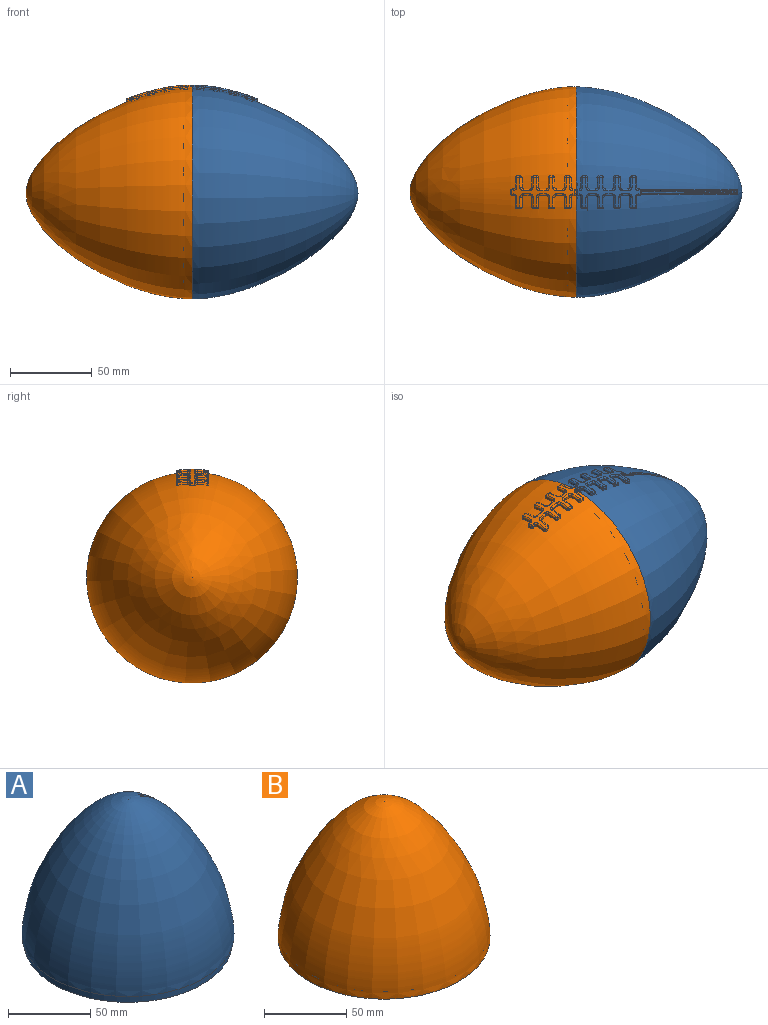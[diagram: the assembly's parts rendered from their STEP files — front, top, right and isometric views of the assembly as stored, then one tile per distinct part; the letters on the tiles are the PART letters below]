
ASSEMBLY  parts=2 mates=1
PART A: 160 faces, bbox 131.7x129.7x107.3 mm
  f0: revolved ~129.02x129.02mm, area 33050.8mm2, adj f1,f83,f84,f85,f86,f87,f88,f89
  f1: bspline ~64.71x52.04mm, area 63.7mm2, adj f0,f2,f83,f159
  f2: plane 59.61x48.72mm, normal (0,1,0), area 17.4mm2, adj f1,f3,f7,f159
  f3: bspline ~63.77x53.46mm, area 64.3mm2, adj f2,f4,f7,f159
  f4: revolved ~58.94x49.24mm, area 78mm2, adj f3,f5,f7,f159
  f5: bspline ~63.77x53.46mm, area 64.2mm2, adj f4,f6,f7,f159
  f6: plane 59.63x48.75mm, normal (0,-1,0), area 17.9mm2, adj f5,f7,f158,f159
  f7: plane 2.57x2.1mm, normal (0,0,1), area 4.8mm2, adj f2,f3,f4,f5,f6,f8,f83,f157
  f8: torus R=55.47mm, axis (0,0,1), area 2.4mm2, adj f7,f9,f81,f82
  f9: revolved ~128.83x128.74mm, area 10804.2mm2, adj f8,f10,f11,f13,f15,f16,f17,f18
  f10: bspline ~2.48x2.39mm, area 3.2mm2, adj f9,f11,f80,f101
  f11: torus R=62mm, axis (0,0,1), area 8.5mm2, adj f9,f10,f12,f102
  f12: sphere r=1mm, area 1.3mm2, adj f11,f13,f103
  f13: bspline ~11.59x3.03mm, area 2.9mm2, adj f9,f12,f14,f104
  f14: sphere r=1mm, area 2.1mm2, adj f13,f15,f105
  f15: torus R=62.34mm, axis (0,0,1), area 10.5mm2, adj f9,f14,f16,f106
  f16: bspline ~2.48x2.37mm, area 3.6mm2, adj f9,f15,f17,f107
  f17: bspline ~11.23x2.39mm, area 6.3mm2, adj f9,f16,f18,f108
  f18: bspline ~2.48x2.38mm, area 3.3mm2, adj f9,f17,f19,f109
  f19: torus R=63.28mm, axis (0,0,1), area 9.1mm2, adj f9,f18,f20,f110
  f20: sphere r=1mm, area 1.4mm2, adj f19,f21,f111
  f21: bspline ~8.41x1.67mm, area 2.9mm2, adj f9,f20,f22,f112
  f22: sphere r=1mm, area 1.5mm2, adj f21,f23,f113
  f23: torus R=63.41mm, axis (0,0,1), area 9.9mm2, adj f9,f22,f24,f114
  f24: bspline ~2.49x2.38mm, area 3.4mm2, adj f9,f23,f25,f115
  f25: bspline ~6.99x1.31mm, area 1.6mm2, adj f9,f24,f26,f116
  f26: sphere r=1mm, area 1.6mm2, adj f25,f27,f117
  f27: torus R=63.5mm, axis (0,0,1), area 3.2mm2, adj f9,f26,f28,f118
  f28: sphere r=1mm, area 1.6mm2, adj f27,f29,f123
  f29: bspline ~6.99x1.32mm, area 1.6mm2, adj f9,f28,f30,f124
  f30: bspline ~2.48x2.38mm, area 3.4mm2, adj f9,f29,f31,f125
  f31: torus R=63.41mm, axis (0,0,1), area 9.9mm2, adj f9,f30,f32,f126
  f32: sphere r=1mm, area 0.9mm2, adj f31,f33,f127
  f33: bspline ~8.41x1.67mm, area 2.9mm2, adj f9,f32,f34,f128
  f34: sphere r=1mm, area 0.9mm2, adj f33,f35,f129
  f35: torus R=63.28mm, axis (0,0,1), area 9.1mm2, adj f9,f34,f36,f130
  f36: bspline ~2.49x2.35mm, area 3.3mm2, adj f9,f35,f37,f131
  f37: bspline ~11.23x2.39mm, area 6.3mm2, adj f9,f36,f38,f132
  f38: bspline ~2.48x2.41mm, area 3.6mm2, adj f9,f37,f39,f133
  f39: torus R=62.34mm, axis (0,0,1), area 10.5mm2, adj f9,f38,f40,f41,f134
  f40: sphere r=1mm, area 0.2mm2, adj f39,f135
  f41: sphere r=1mm, area 0.5mm2, adj f39,f42,f135
  f42: bspline ~16.12x3.5mm, area 2.9mm2, adj f9,f41,f43,f136
  f43: sphere r=1mm, area 1.9mm2, adj f42,f44,f137
  f44: torus R=62mm, axis (0,0,1), area 8.5mm2, adj f9,f43,f45,f138
  f45: bspline ~2.48x2.31mm, area 3.2mm2, adj f9,f44,f46,f139
  f46: bspline ~16.6x4.38mm, area 6.4mm2, adj f9,f45,f47,f140
  f47: bspline ~2.48x2.45mm, area 3.7mm2, adj f9,f46,f48,f141
  f48: torus R=60.26mm, axis (0,0,1), area 11.1mm2, adj f9,f47,f49,f142
  f49: sphere r=1mm, area 1.1mm2, adj f48,f50,f143
  f50: bspline ~16.79x5.21mm, area 3mm2, adj f9,f49,f51,f144
  f51: sphere r=1mm, area 0.7mm2, adj f50,f52,f145
  f52: torus R=59.73mm, axis (0,0,1), area 7.9mm2, adj f9,f51,f53,f146
  f53: bspline ~2.47x2.27mm, area 3.2mm2, adj f9,f52,f54,f147
  f54: bspline ~13.75x5.14mm, area 6.5mm2, adj f9,f53,f55,f148
  f55: bspline ~2.56x2.16mm, area 3.9mm2, adj f9,f54,f56,f149
  f56: torus R=57.27mm, axis (0,0,1), area 11.6mm2, adj f9,f55,f57,f58,f150
  f57: sphere r=1mm, area 0.2mm2, adj f56,f151
  f58: sphere r=1mm, area 0.6mm2, adj f56,f59,f151
  f59: bspline ~13.84x5.73mm, area 3mm2, adj f9,f58,f60,f152
  f60: sphere r=1mm, area 0.6mm2, adj f59,f61,f153
  f61: torus R=56.57mm, axis (0,0,1), area 7.5mm2, adj f9,f60,f62,f154
  f62: bspline ~2.46x2.21mm, area 3.2mm2, adj f9,f61,f63,f155
  f63: bspline ~14.01x6.1mm, area 1.6mm2, adj f9,f62,f82,f156
  f64: bspline ~10.36x4.85mm, area 1.6mm2, adj f9,f65,f81,f84
  f65: bspline ~2.5x2.44mm, area 3.2mm2, adj f9,f64,f66,f85
  f66: torus R=56.57mm, axis (0,0,1), area 7.5mm2, adj f9,f65,f67,f86
  f67: sphere r=1mm, area 0.8mm2, adj f66,f68,f87
  f68: bspline ~13.84x5.73mm, area 3mm2, adj f9,f67,f69,f88
  f69: sphere r=1mm, area 1.6mm2, adj f68,f70,f89
  f70: torus R=57.27mm, axis (0,0,1), area 11.6mm2, adj f9,f69,f71,f90
  f71: bspline ~2.48x2.47mm, area 3.9mm2, adj f9,f70,f72,f91
  f72: bspline ~13.75x5.14mm, area 6.5mm2, adj f9,f71,f73,f92
  f73: bspline ~2.49x2.41mm, area 3.2mm2, adj f9,f72,f74,f93
  f74: torus R=59.73mm, axis (0,0,1), area 7.9mm2, adj f9,f73,f75,f94
  f75: sphere r=1mm, area 1.2mm2, adj f74,f76,f95
  f76: bspline ~16.79x5.21mm, area 3mm2, adj f9,f75,f77,f96
  f77: sphere r=1mm, area 1.6mm2, adj f76,f78,f97
  f78: torus R=60.26mm, axis (0,0,1), area 11.1mm2, adj f9,f77,f79,f98
  f79: bspline ~2.48x2.42mm, area 3.7mm2, adj f9,f78,f80,f99
  f80: bspline ~16.6x4.38mm, area 6.4mm2, adj f9,f10,f79,f100
  f81: sphere r=1mm, area 0.9mm2, adj f8,f64,f83
  f82: sphere r=1mm, area 1.3mm2, adj f8,f63,f157
  f83: cylinder r=1mm len=1.86mm, axis (1,0,0), area 2mm2, adj f0,f1,f7,f81,f84
  f84: plane 1.32x0.96mm, normal (0,-1,0), area 0.9mm2, adj f0,f64,f83,f85
  f85: cylinder r=1mm len=1.62mm, axis (1,0,0), area 1.8mm2, adj f0,f65,f84,f86
  f86: plane 6x1.93mm, normal (0,0,1), area 7.8mm2, adj f0,f66,f85,f87
  f87: cylinder r=1mm len=1.29mm, axis (-1,0,0), area 1.9mm2, adj f0,f67,f86,f88
  f88: plane 2x1.81mm, normal (0,-1,0), area 2.2mm2, adj f0,f68,f87,f89
  f89: cylinder r=1mm len=1.1mm, axis (-1,0,0), area 1.3mm2, adj f0,f69,f88,f90
  f90: plane 6x1.22mm, normal (0,0,-1), area 3.6mm2, adj f0,f70,f89,f91
  f91: cylinder r=1mm len=1.34mm, axis (1,0,0), area 1.2mm2, adj f0,f71,f90,f92
  f92: plane 4.01x2.21mm, normal (0,-1,0), area 3.9mm2, adj f0,f72,f91,f93
  f93: cylinder r=1mm len=1.48mm, axis (1,0,0), area 1.7mm2, adj f0,f73,f92,f94
  f94: plane 6x1.84mm, normal (0,0,1), area 7.4mm2, adj f0,f74,f93,f95
  f95: cylinder r=1mm len=1.23mm, axis (-1,0,0), area 1.8mm2, adj f0,f75,f94,f96
  f96: plane 2x1.65mm, normal (0,-1,0), area 2.2mm2, adj f0,f76,f95,f97
  f97: cylinder r=1mm len=1.11mm, axis (-1,0,0), area 1.4mm2, adj f0,f77,f96,f98
  f98: plane 6x1.31mm, normal (0,0,-1), area 4.3mm2, adj f0,f78,f97,f99
  f99: cylinder r=1mm len=1.28mm, axis (1,0,0), area 1.3mm2, adj f0,f79,f98,f100
  f100: plane 4.01x1.88mm, normal (0,-1,0), area 4mm2, adj f0,f80,f99,f101
  f101: cylinder r=1mm len=1.32mm, axis (1,0,0), area 1.7mm2, adj f0,f10,f100,f102
  f102: plane 6x1.74mm, normal (0,0,1), area 7mm2, adj f0,f11,f101,f103
  f103: cylinder r=1mm len=1.16mm, axis (-1,0,0), area 1.8mm2, adj f0,f12,f102,f104
  f104: plane 2x1.47mm, normal (0,-1,0), area 2.3mm2, adj f0,f13,f103,f105
  f105: cylinder r=1mm len=1.13mm, axis (-1,0,0), area 1.5mm2, adj f0,f14,f104,f106
  f106: plane 6x1.4mm, normal (0,0,-1), area 5mm2, adj f0,f15,f105,f107
  f107: cylinder r=1mm len=1.2mm, axis (1,0,0), area 1.5mm2, adj f0,f16,f106,f108
  f108: plane 4.02x1.5mm, normal (0,-1,0), area 4.1mm2, adj f0,f17,f107,f109
  f109: cylinder r=1mm len=1.13mm, axis (1,0,0), area 1.6mm2, adj f0,f18,f108,f110
  f110: plane 6x1.64mm, normal (0,0,1), area 6.4mm2, adj f0,f19,f109,f111
  f111: cylinder r=1mm len=1.14mm, axis (-1,0,0), area 1.7mm2, adj f0,f20,f110,f112
  f112: plane 2.04x1.27mm, normal (0,-1,0), area 2.3mm2, adj f0,f21,f111,f113
  f113: cylinder r=1mm len=1.14mm, axis (-1,0,0), area 1.6mm2, adj f0,f22,f112,f114
  f114: plane 6x1.52mm, normal (0,0,-1), area 5.7mm2, adj f0,f23,f113,f115
  f115: cylinder r=1mm len=1.09mm, axis (1,0,0), area 1.6mm2, adj f0,f24,f114,f116
  f116: plane 1.04x1mm, normal (0,-1,0), area 1mm2, adj f0,f25,f115,f117
  f117: cylinder r=1mm len=1.02mm, axis (-1,0,0), area 1.6mm2, adj f0,f26,f116,f118
  f118: plane 130.01x129.02mm, normal (0,0,-1), area 404.2mm2, adj f0,f27,f117,f119,f123
  f119: cylinder r=63.51mm len=127.02mm, axis (0,0,1), area 1995.2mm2, adj f118,f120
  f120: plane 127.02x127.02mm, normal (0,0,-1), area 395.9mm2, adj f119,f121
  f121: cylinder r=62.51mm len=125.02mm, axis (0,0,1), area 1963.8mm2, adj f120,f122
  f122: revolved ~125.02x62.51mm, area 0mm2, adj f121
  f123: cylinder r=1mm len=1.02mm, axis (1,0,0), area 1.6mm2, adj f0,f28,f118,f124
  f124: plane 1.04x1.04mm, normal (0,1,0), area 1.1mm2, adj f0,f29,f123,f125
  f125: cylinder r=1mm len=1.09mm, axis (1,0,0), area 1.6mm2, adj f0,f30,f124,f126
  f126: plane 6x1.52mm, normal (0,0,-1), area 5.7mm2, adj f0,f31,f125,f127
  f127: cylinder r=1mm len=1.14mm, axis (-1,0,0), area 1.6mm2, adj f0,f32,f126,f128
  f128: plane 2x1.27mm, normal (0,1,0), area 2.3mm2, adj f0,f33,f127,f129
  f129: cylinder r=1mm len=1.14mm, axis (-1,0,0), area 1.7mm2, adj f0,f34,f128,f130
  f130: plane 6x1.64mm, normal (0,0,1), area 6.4mm2, adj f0,f35,f129,f131
  f131: cylinder r=1mm len=1.13mm, axis (1,0,0), area 1.6mm2, adj f0,f36,f130,f132
  f132: plane 4.02x1.5mm, normal (0,1,0), area 4.1mm2, adj f0,f37,f131,f133
  f133: cylinder r=1mm len=1.2mm, axis (1,0,0), area 1.5mm2, adj f0,f38,f132,f134
  f134: plane 6x1.4mm, normal (0,0,-1), area 5mm2, adj f0,f39,f133,f135
  f135: cylinder r=1mm len=1.13mm, axis (-1,0,0), area 1.5mm2, adj f0,f40,f41,f134,f136
  f136: plane 2x1.47mm, normal (0,1,0), area 2.3mm2, adj f0,f42,f135,f137
  f137: cylinder r=1mm len=1.16mm, axis (-1,0,0), area 1.8mm2, adj f0,f43,f136,f138
  f138: plane 6x1.74mm, normal (0,0,1), area 7mm2, adj f0,f44,f137,f139
  f139: cylinder r=1mm len=1.32mm, axis (1,0,0), area 1.7mm2, adj f0,f45,f138,f140
  f140: plane 4.01x1.88mm, normal (0,1,0), area 4mm2, adj f0,f46,f139,f141
  f141: cylinder r=1mm len=1.28mm, axis (1,0,0), area 1.3mm2, adj f0,f47,f140,f142
  f142: plane 6x1.31mm, normal (0,0,-1), area 4.3mm2, adj f0,f48,f141,f143
  f143: cylinder r=1mm len=1.11mm, axis (-1,0,0), area 1.4mm2, adj f0,f49,f142,f144
  f144: plane 2x1.65mm, normal (0,1,0), area 2.2mm2, adj f0,f50,f143,f145
  f145: cylinder r=1mm len=1.23mm, axis (-1,0,0), area 1.8mm2, adj f0,f51,f144,f146
  f146: plane 6x1.84mm, normal (0,0,1), area 7.4mm2, adj f0,f52,f145,f147
  f147: cylinder r=1mm len=1.48mm, axis (1,0,0), area 1.7mm2, adj f0,f53,f146,f148
  f148: plane 4.01x2.21mm, normal (0,1,0), area 3.9mm2, adj f0,f54,f147,f149
  f149: cylinder r=1mm len=1.34mm, axis (1,0,0), area 1.2mm2, adj f0,f55,f148,f150
  f150: plane 6x1.22mm, normal (0,0,-1), area 3.6mm2, adj f0,f56,f149,f151
  f151: cylinder r=1mm len=1.1mm, axis (-1,0,0), area 1.3mm2, adj f0,f57,f58,f150,f152
  f152: plane 2x1.81mm, normal (0,1,0), area 2.2mm2, adj f0,f59,f151,f153
  f153: cylinder r=1mm len=1.29mm, axis (-1,0,0), area 1.9mm2, adj f0,f60,f152,f154
  f154: plane 6x1.93mm, normal (0,0,1), area 7.8mm2, adj f0,f61,f153,f155
  f155: cylinder r=1mm len=1.62mm, axis (1,0,0), area 1.8mm2, adj f0,f62,f154,f156
  f156: plane 1.32x0.96mm, normal (0,1,0), area 0.9mm2, adj f0,f63,f155,f157
  f157: cylinder r=1mm len=1.86mm, axis (-1,0,0), area 2mm2, adj f0,f7,f82,f156,f158
  f158: bspline ~64.71x52.04mm, area 63.7mm2, adj f0,f6,f157,f159
  f159: plane 5.4x3.7mm, normal (0,0,-1), area 9.4mm2, adj f0,f1,f2,f3,f4,f5,f6,f158
PART B: 149 faces, bbox 131x129x101.6 mm
  f0: revolved ~129.02x129.02mm, area 33283.8mm2, adj f1,f75,f76,f77,f78,f79,f80,f81
  f1: cylinder r=1mm len=1.32mm, axis (1,0,0), area 1.8mm2, adj f0,f2,f75,f147
  f2: sphere r=1mm, area 1.3mm2, adj f1,f3,f74
  f3: torus R=55.47mm, axis (0,0,1), area 2.4mm2, adj f2,f4,f73,f147
  f4: revolved ~128.83x128.74mm, area 10801.2mm2, adj f3,f5,f6,f7,f8,f10,f12,f13
  f5: bspline ~2.42x2.15mm, area 3.7mm2, adj f4,f6,f72,f90
  f6: bspline ~16.6x4.37mm, area 6.4mm2, adj f4,f5,f7,f91
  f7: bspline ~2.48x2.39mm, area 3.2mm2, adj f4,f6,f8,f92
  f8: torus R=62.01mm, axis (0,0,1), area 8.5mm2, adj f4,f7,f9,f93
  f9: sphere r=1mm, area 1.3mm2, adj f8,f10,f94
  f10: bspline ~11.59x3.03mm, area 2.9mm2, adj f4,f9,f11,f95
  f11: sphere r=1mm, area 1.5mm2, adj f10,f12,f96
  f12: torus R=62.35mm, axis (0,0,1), area 10.5mm2, adj f4,f11,f13,f97
  f13: bspline ~2.48x2.37mm, area 3.6mm2, adj f4,f12,f14,f98
  f14: bspline ~11.22x2.39mm, area 6.3mm2, adj f4,f13,f15,f99
  f15: bspline ~2.38x2.14mm, area 3.3mm2, adj f4,f14,f16,f100
  f16: torus R=63.29mm, axis (0,0,1), area 9.1mm2, adj f4,f15,f17,f101
  f17: sphere r=1mm, area 1.4mm2, adj f16,f18,f102
  f18: bspline ~8.41x1.67mm, area 2.9mm2, adj f4,f17,f19,f103
  f19: sphere r=1mm, area 1.5mm2, adj f18,f20,f104
  f20: torus R=63.41mm, axis (0,0,1), area 9.9mm2, adj f4,f19,f21,f105
  f21: bspline ~2.49x2.38mm, area 3.4mm2, adj f4,f20,f22,f106
  f22: bspline ~6.99x1.31mm, area 1.6mm2, adj f4,f21,f23,f107
  f23: sphere r=1mm, area 1.6mm2, adj f22,f24,f108
  f24: torus R=63.5mm, axis (0,0,1), area 3.2mm2, adj f4,f23,f25,f109
  f25: sphere r=1mm, area 1.6mm2, adj f24,f26,f112
  f26: bspline ~6.99x1.31mm, area 1.6mm2, adj f4,f25,f27,f113
  f27: bspline ~2.48x2.38mm, area 3.4mm2, adj f4,f26,f28,f114
  f28: torus R=63.41mm, axis (0,0,1), area 9.9mm2, adj f4,f27,f29,f115
  f29: sphere r=1mm, area 1.5mm2, adj f28,f30,f116
  f30: bspline ~8.41x1.67mm, area 2.9mm2, adj f4,f29,f31,f117
  f31: sphere r=1mm, area 1.4mm2, adj f30,f32,f118
  f32: torus R=63.29mm, axis (0,0,1), area 9.1mm2, adj f4,f31,f33,f119
  f33: bspline ~2.49x2.35mm, area 3.3mm2, adj f4,f32,f34,f120
  f34: bspline ~11.22x2.39mm, area 6.3mm2, adj f4,f33,f35,f121
  f35: bspline ~2.48x2.41mm, area 3.6mm2, adj f4,f34,f36,f122
  f36: torus R=62.35mm, axis (0,0,1), area 10.5mm2, adj f4,f35,f37,f123
  f37: sphere r=1mm, area 1.5mm2, adj f36,f38,f124
  f38: bspline ~16.12x3.5mm, area 2.9mm2, adj f4,f37,f39,f125
  f39: sphere r=1mm, area 1.3mm2, adj f38,f40,f126
  f40: torus R=62.01mm, axis (0,0,1), area 8.5mm2, adj f4,f39,f41,f127
  f41: bspline ~2.48x2.31mm, area 3.2mm2, adj f4,f40,f42,f128
  f42: bspline ~16.6x4.37mm, area 6.4mm2, adj f4,f41,f43,f129
  f43: bspline ~2.48x2.45mm, area 3.7mm2, adj f4,f42,f44,f130
  f44: torus R=60.27mm, axis (0,0,1), area 11.1mm2, adj f4,f43,f45,f131
  f45: sphere r=1mm, area 1.7mm2, adj f44,f46,f132
  f46: bspline ~16.78x5.21mm, area 3mm2, adj f4,f45,f47,f133
  f47: sphere r=1mm, area 1.3mm2, adj f46,f48,f134
  f48: torus R=59.74mm, axis (0,0,1), area 7.9mm2, adj f4,f47,f49,f135
  f49: bspline ~2.47x2.27mm, area 3.2mm2, adj f4,f48,f50,f136
  f50: bspline ~13.75x5.14mm, area 6.5mm2, adj f4,f49,f51,f137
  f51: bspline ~2.56x2.16mm, area 3.9mm2, adj f4,f50,f52,f138
  f52: torus R=57.28mm, axis (0,0,1), area 11.6mm2, adj f4,f51,f53,f139
  f53: sphere r=1mm, area 1.6mm2, adj f52,f54,f140
  f54: bspline ~13.84x5.73mm, area 3mm2, adj f4,f53,f55,f141
  f55: sphere r=1mm, area 1.2mm2, adj f54,f56,f142
  f56: torus R=56.58mm, axis (0,0,1), area 7.5mm2, adj f4,f55,f57,f143
  f57: bspline ~2.46x2.21mm, area 3.2mm2, adj f4,f56,f58,f144
  f58: bspline ~14.01x6.09mm, area 1.7mm2, adj f4,f57,f73,f145
  f59: bspline ~2.5x2.44mm, area 3.2mm2, adj f4,f60,f74,f76
  f60: torus R=56.58mm, axis (0,0,1), area 7.5mm2, adj f4,f59,f61,f77
  f61: sphere r=1mm, area 1.2mm2, adj f60,f62,f78
  f62: bspline ~13.84x5.73mm, area 3mm2, adj f4,f61,f63,f79
  f63: sphere r=1mm, area 1.6mm2, adj f62,f64,f80
  f64: torus R=57.28mm, axis (0,0,1), area 11.6mm2, adj f4,f63,f65,f81
  f65: bspline ~2.48x2.47mm, area 3.9mm2, adj f4,f64,f66,f82
  f66: bspline ~13.75x5.14mm, area 6.5mm2, adj f4,f65,f67,f83
  f67: bspline ~2.49x2.41mm, area 3.2mm2, adj f4,f66,f68,f84
  f68: torus R=59.74mm, axis (0,0,1), area 7.9mm2, adj f4,f67,f69,f85
  f69: sphere r=1mm, area 1.2mm2, adj f68,f70,f86
  f70: bspline ~16.78x5.21mm, area 3mm2, adj f4,f69,f71,f87
  f71: sphere r=1mm, area 1.6mm2, adj f70,f72,f88
  f72: torus R=60.27mm, axis (0,0,1), area 11.1mm2, adj f4,f5,f71,f89
  f73: sphere r=1mm, area 1.3mm2, adj f3,f58,f146
  f74: bspline ~10.35x4.85mm, area 1.7mm2, adj f2,f4,f59,f75
  f75: plane 1.34x1mm, normal (0,-1,0), area 1mm2, adj f0,f1,f74,f76
  f76: cylinder r=1mm len=1.63mm, axis (1,0,0), area 2mm2, adj f0,f59,f75,f77
  f77: plane 6x1.93mm, normal (0,0,1), area 7.8mm2, adj f0,f60,f76,f78
  f78: cylinder r=1mm len=1.32mm, axis (-1,0,0), area 2mm2, adj f0,f61,f77,f79
  f79: plane 2x1.8mm, normal (0,-1,0), area 2.2mm2, adj f0,f62,f78,f80
  f80: cylinder r=1mm len=1.1mm, axis (-1,0,0), area 1.3mm2, adj f0,f63,f79,f81
  f81: plane 6x1.22mm, normal (0,0,-1), area 3.6mm2, adj f0,f64,f80,f82
  f82: cylinder r=1mm len=1.34mm, axis (1,0,0), area 1.1mm2, adj f0,f65,f81,f83
  f83: plane 4.01x2.21mm, normal (0,-1,0), area 3.9mm2, adj f0,f66,f82,f84
  f84: cylinder r=1mm len=1.49mm, axis (1,0,0), area 1.9mm2, adj f0,f67,f83,f85
  f85: plane 6x1.84mm, normal (0,0,1), area 7.4mm2, adj f0,f68,f84,f86
  f86: cylinder r=1mm len=1.23mm, axis (-1,0,0), area 1.8mm2, adj f0,f69,f85,f87
  f87: plane 2x1.65mm, normal (0,-1,0), area 2.2mm2, adj f0,f70,f86,f88
  f88: cylinder r=1mm len=1.11mm, axis (-1,0,0), area 1.4mm2, adj f0,f71,f87,f89
  f89: plane 6x1.31mm, normal (0,0,-1), area 4.3mm2, adj f0,f72,f88,f90
  f90: cylinder r=1mm len=1.28mm, axis (1,0,0), area 1.3mm2, adj f0,f5,f89,f91
  f91: plane 4.01x1.88mm, normal (0,-1,0), area 4mm2, adj f0,f6,f90,f92
  f92: cylinder r=1mm len=1.33mm, axis (1,0,0), area 1.8mm2, adj f0,f7,f91,f93
  f93: plane 6x1.74mm, normal (0,0,1), area 7mm2, adj f0,f8,f92,f94
  f94: cylinder r=1mm len=1.16mm, axis (-1,0,0), area 1.8mm2, adj f0,f9,f93,f95
  f95: plane 2x1.47mm, normal (0,-1,0), area 2.3mm2, adj f0,f10,f94,f96
  f96: cylinder r=1mm len=1.13mm, axis (-1,0,0), area 1.5mm2, adj f0,f11,f95,f97
  f97: plane 6x1.4mm, normal (0,0,-1), area 5mm2, adj f0,f12,f96,f98
  f98: cylinder r=1mm len=1.2mm, axis (1,0,0), area 1.5mm2, adj f0,f13,f97,f99
  f99: plane 4.02x1.5mm, normal (0,-1,0), area 4.1mm2, adj f0,f14,f98,f100
  f100: cylinder r=1mm len=1.13mm, axis (1,0,0), area 1.6mm2, adj f0,f15,f99,f101
  f101: plane 6x1.64mm, normal (0,0,1), area 6.4mm2, adj f0,f16,f100,f102
  f102: cylinder r=1mm len=1.14mm, axis (-1,0,0), area 1.7mm2, adj f0,f17,f101,f103
  f103: plane 2x1.27mm, normal (0,-1,0), area 2.3mm2, adj f0,f18,f102,f104
  f104: cylinder r=1mm len=1.14mm, axis (-1,0,0), area 1.6mm2, adj f0,f19,f103,f105
  f105: plane 6x1.52mm, normal (0,0,-1), area 5.7mm2, adj f0,f20,f104,f106
  f106: cylinder r=1mm len=1.09mm, axis (1,0,0), area 1.6mm2, adj f0,f21,f105,f107
  f107: plane 1.04x1mm, normal (0,-1,0), area 1mm2, adj f0,f22,f106,f108
  f108: cylinder r=1mm len=1.02mm, axis (-1,0,0), area 1.6mm2, adj f0,f23,f107,f109
  f109: plane 130.01x129.02mm, normal (0,0,-1), area 404.2mm2, adj f0,f24,f108,f110,f112
  f110: cylinder r=63.51mm len=127.02mm, axis (0,0,1), area 1995.2mm2, adj f109,f111
  f111: cone r=63.51mm half-angle=89deg, axis (0,0,1), area 457.8mm2, adj f110
  f112: cylinder r=1mm len=1.02mm, axis (1,0,0), area 1.6mm2, adj f0,f25,f109,f113
  f113: plane 1.04x1mm, normal (0,1,0), area 1mm2, adj f0,f26,f112,f114
  f114: cylinder r=1mm len=1.09mm, axis (1,0,0), area 1.6mm2, adj f0,f27,f113,f115
  f115: plane 6x1.52mm, normal (0,0,-1), area 5.7mm2, adj f0,f28,f114,f116
  f116: cylinder r=1mm len=1.14mm, axis (-1,0,0), area 1.6mm2, adj f0,f29,f115,f117
  f117: plane 2x1.27mm, normal (0,1,0), area 2.3mm2, adj f0,f30,f116,f118
  f118: cylinder r=1mm len=1.14mm, axis (-1,0,0), area 1.7mm2, adj f0,f31,f117,f119
  f119: plane 6x1.64mm, normal (0,0,1), area 6.4mm2, adj f0,f32,f118,f120
  f120: cylinder r=1mm len=1.13mm, axis (1,0,0), area 1.6mm2, adj f0,f33,f119,f121
  f121: plane 4.02x1.5mm, normal (0,1,0), area 4.1mm2, adj f0,f34,f120,f122
  f122: cylinder r=1mm len=1.2mm, axis (1,0,0), area 1.5mm2, adj f0,f35,f121,f123
  f123: plane 6x1.4mm, normal (0,0,-1), area 5mm2, adj f0,f36,f122,f124
  f124: cylinder r=1mm len=1.13mm, axis (-1,0,0), area 1.5mm2, adj f0,f37,f123,f125
  f125: plane 2x1.47mm, normal (0,1,0), area 2.3mm2, adj f0,f38,f124,f126
  f126: cylinder r=1mm len=1.16mm, axis (-1,0,0), area 1.8mm2, adj f0,f39,f125,f127
  f127: plane 6x1.74mm, normal (0,0,1), area 7mm2, adj f0,f40,f126,f128
  f128: cylinder r=1mm len=1.33mm, axis (1,0,0), area 1.8mm2, adj f0,f41,f127,f129
  f129: plane 4.01x1.88mm, normal (0,1,0), area 4mm2, adj f0,f42,f128,f130
  f130: cylinder r=1mm len=1.28mm, axis (1,0,0), area 1.3mm2, adj f0,f43,f129,f131
  f131: plane 6x1.31mm, normal (0,0,-1), area 4.3mm2, adj f0,f44,f130,f132
  f132: cylinder r=1mm len=1.11mm, axis (-1,0,0), area 1.4mm2, adj f0,f45,f131,f133
  f133: plane 2x1.65mm, normal (0,1,0), area 2.2mm2, adj f0,f46,f132,f134
  f134: cylinder r=1mm len=1.23mm, axis (-1,0,0), area 1.8mm2, adj f0,f47,f133,f135
  f135: plane 6x1.84mm, normal (0,0,1), area 7.4mm2, adj f0,f48,f134,f136
  f136: cylinder r=1mm len=1.49mm, axis (1,0,0), area 1.9mm2, adj f0,f49,f135,f137
  f137: plane 4.01x2.21mm, normal (0,1,0), area 3.9mm2, adj f0,f50,f136,f138
  f138: cylinder r=1mm len=1.34mm, axis (1,0,0), area 1.1mm2, adj f0,f51,f137,f139
  f139: plane 6x1.22mm, normal (0,0,-1), area 3.6mm2, adj f0,f52,f138,f140
  f140: cylinder r=1mm len=1.1mm, axis (-1,0,0), area 1.3mm2, adj f0,f53,f139,f141
  f141: plane 2x1.8mm, normal (0,1,0), area 2.2mm2, adj f0,f54,f140,f142
  f142: cylinder r=1mm len=1.32mm, axis (-1,0,0), area 2mm2, adj f0,f55,f141,f143
  f143: plane 6x1.93mm, normal (0,0,1), area 7.8mm2, adj f0,f56,f142,f144
  f144: cylinder r=1mm len=1.63mm, axis (1,0,0), area 2mm2, adj f0,f57,f143,f145
  f145: plane 1.34x1mm, normal (0,1,0), area 1mm2, adj f0,f58,f144,f146
  f146: cylinder r=1mm len=1.32mm, axis (-1,0,0), area 1.8mm2, adj f0,f73,f145,f147
  f147: plane 2x1.32mm, normal (0,0,1), area 2.6mm2, adj f0,f1,f3,f146
  f148: revolved ~124.7x62.35mm, area 0mm2
PLACE A rot(axis=(-0.71,0,-0.71),179.8deg) t=(77.47,-106.29,147.61)mm
PLACE B rot(axis=(0,-1,0),90deg) t=(77.47,-106.29,147.61)mm
MATE parallel B.f110 <-> A.f119  axis (1,0,0) through (77.47,-106.29,147.61)mm
